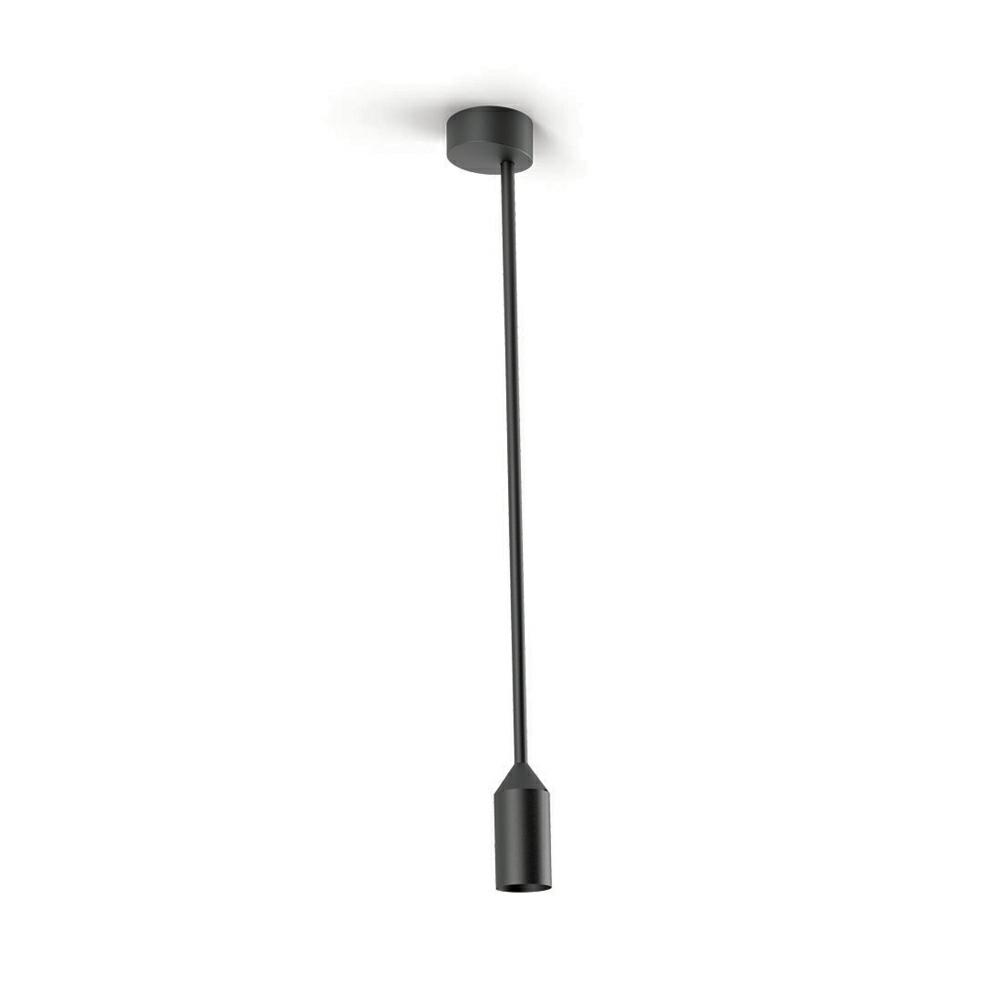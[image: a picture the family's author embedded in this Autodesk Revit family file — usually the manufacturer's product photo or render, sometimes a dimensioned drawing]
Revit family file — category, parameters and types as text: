
# Revit family: Platek_Flamingo_Downlight
name_source: partatom
category: Apparecchi per illuminazione
revit_build: Autodesk Revit 2017 (Build: 20160225_1515(x64)
units: mm (PartAtom-declared; Revit-internal decimal feet)

## family parameters
Basato su piano di lavoro = No
Condiviso = No
Punto di calcolo locali = No
Quota connettore circolare = Usa diametro
Sempre verticale = Sì
Sorgente d'illuminazione = Sì
Taglio con vuoti quando caricato = No
Tipo di parte = Normale

## types (2) — shared parameters
Angolo inclinazione = 90.00°
Beam Angle = 76.00°
CRI = >80
Cable Lenght = 0,1 (2x1 mm²)
Carico apparente = 0 VA
Colour Temperature = 3000 K
Commenti sul tipo = Suitable for restaurants, balconies, terraces, lounge areas, hall
Descrizione = Outdoor lighting, downlight, ceiling mounted
Diffuse Type = Polycarbonate
Dimmable = No
Emetti da diametro cerchio = 25 mm  [stored 0.082021 ft]
Energy Efficiency Rating = A/A+/A++
Filtro dei colori = 16777215
Frequency = 50/60 Hz
IK Rating = IK 06
IP Rating = IP65
Insulation Class = 1
LED Protection = Surge protection included
Lampada = LED
Light Source = PLK_Light Source
Luminaire Luminous Flux = 385 lm
Luminaire Luminous Intensity = 259 cd
Luminaire Wattage = 9 W
Manufacturer Comment = IP68 Connector Included
Modello = Flamingo Downlight
Nota chiave = Other Led colors available on request
Power Supply Unit = Included
Product Documentation Link = http://www.platek.eu
Product Page URL = http://www.platek.eu
Produttore = PLATEK SRL
Rendi la forma visibile nel rendering = No
Supply Voltage = 230 V
Supply Voltage Max = 240 V
Supply Voltage Min = 220 V
URL = www.platek.eu
Variazione temperatura colore lampada con luminosità attenuata = <Nessuno>

## per-type parameters (varying)
| type | Body | Codice assieme | File diagramma fotometrico | H. | H.170.000_800.000 | Immagine tipo | Mounting Type | PLATEK Article Code | Product Dimension | Stem. | Stem.0.698_629.999 |
| 3070216_9W_LED_3000K_H800mm | PLK_Aluminium_Black | 3070216.01(Black); 3070216.09(Bronze) | 3070216.IES | 800 mm  [stored 2.62467 ft] | No | flamingo_downlight_800.jpg | ceiling mounted | 3270216 | L85m x H800m | 629.999 mm  [stored 2.06693 ft] | No |
| 3070116_9W_LED_3000K_H170mm | PLK_Black | 3070116.01(Black); 3070116.09(Bronze) | 3070116.IES | 170 mm  [stored 0.557743 ft] | Sì | flamingo_downlight_170.jpg | Table | 3270116 | D85mm x H170mm | 0.698 mm  [stored 0.00229003 ft] | Sì |

note: [stored X ft] marks values corroborated as IEEE doubles in the binary element streams (Revit-internal decimal feet)
